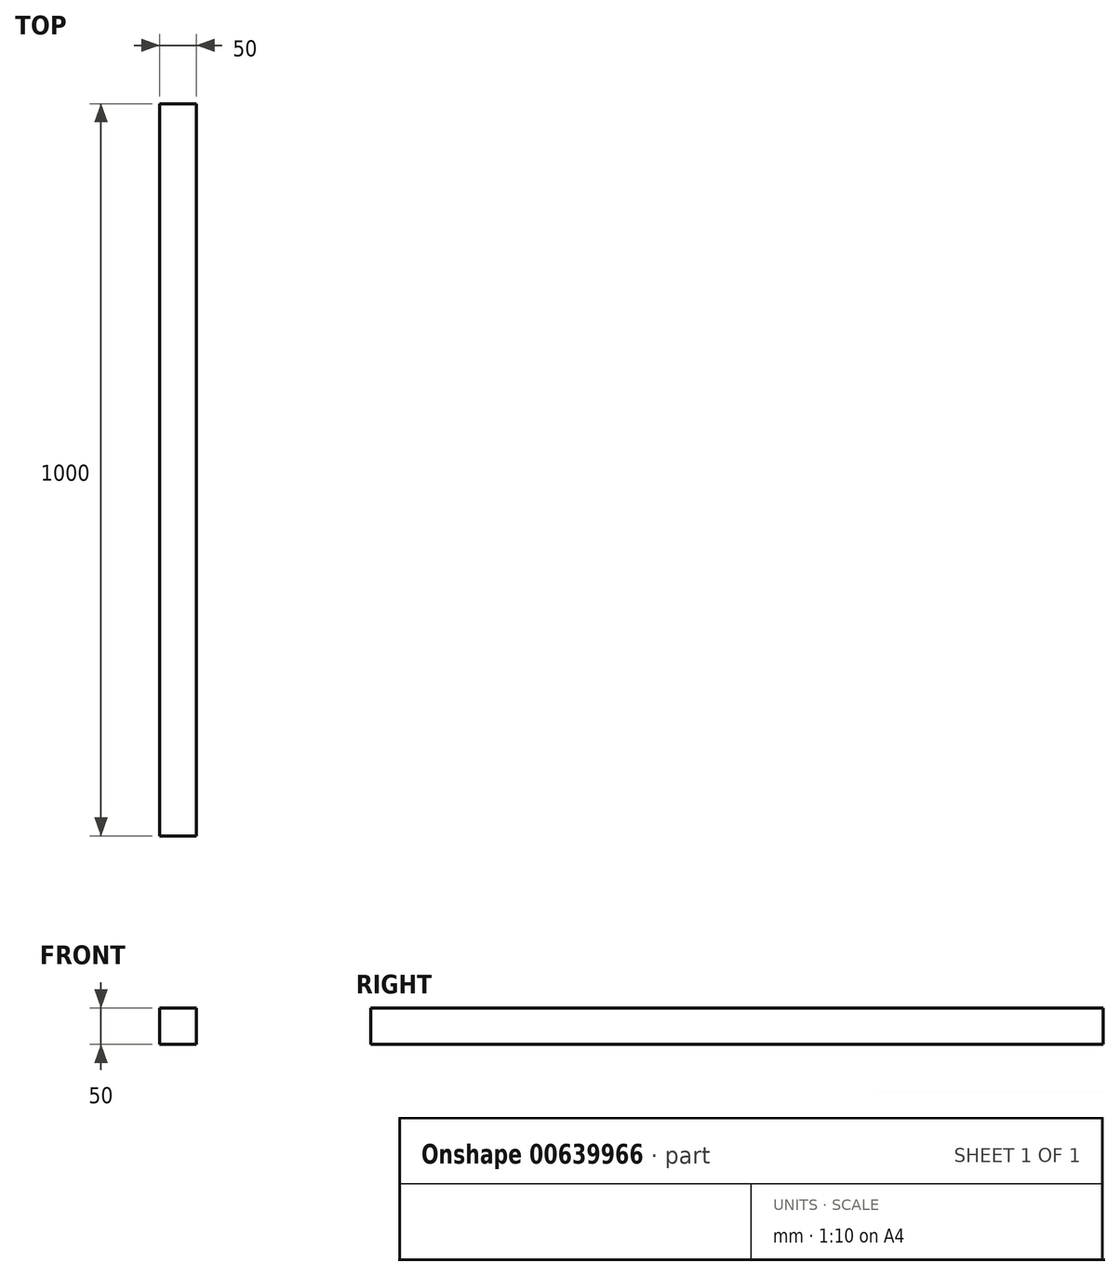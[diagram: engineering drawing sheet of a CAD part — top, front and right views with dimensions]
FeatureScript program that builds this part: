
annotation { "Feature Type Name" : "Feature", "Feature Type Description" : "" }
export const myFeature = defineFeature(function(context is Context, id is Id, definition is map)
    precondition{}
    {
        {
            var Q0;
            Q0=qCreatedBy(makeId("Top.planeOp"),FACE);
            var sketch = newSketch(context, id + "F0", { "sketchPlane" : qUnion([Q0])});
            skLineSegment(sketch, "E0", {"start": v(0, 0) * mm, "end": v(50, 0) * mm});
            skLineSegment(sketch, "E1", {"start": v(0, 0) * mm, "end": v(0, -1000) * mm});
            skLineSegment(sketch, "E2", {"start": v(50, 0) * mm, "end": v(50, -1000) * mm});
            skLineSegment(sketch, "E3", {"start": v(0, -1000) * mm, "end": v(50, -1000) * mm});
            skSolve(sketch);
        }
        {
            var Q0;
            Q0=makeQuery(id+"F0.imprint","IMPRINT",FACE,{"disambiguationData":[TD([[makeQuery(id+"F0.imprint","IMPRINT",EDGE,{"derivedFrom":sQuery(id+"F0.wireOp",EDGE,"E0")}),-1.0]])]});
            extrude(context, id + "F1", {"entities" : qUnion([Q0]), "depth" : 50 * mm, "offsetDistance" : 25 * mm});
        }
    });
